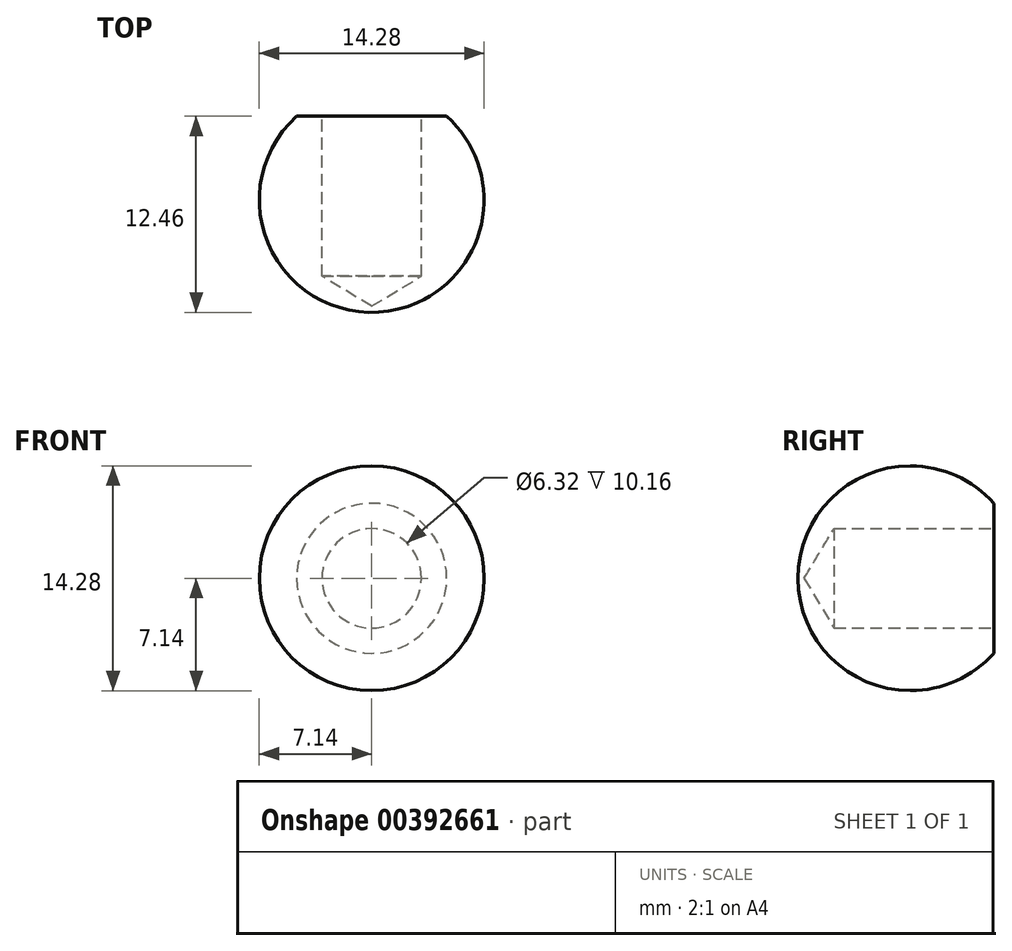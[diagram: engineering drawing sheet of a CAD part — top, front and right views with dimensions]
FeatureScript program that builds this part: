
annotation { "Feature Type Name" : "Feature", "Feature Type Description" : "" }
export const myFeature = defineFeature(function(context is Context, id is Id, definition is map)
    precondition{}
    {
        {
            var Q0;
            Q0=qCreatedBy(makeId("Front.planeOp"),FACE);
            var sketch = newSketch(context, id + "F0", { "sketchPlane" : qUnion([Q0])});
            skArc(sketch, "E0", {"start": v(0, -7.14) * mm, "mid": v(7.14, 0) * mm, "end": v(0, 7.14) * mm});
            skLineSegment(sketch, "E1", {"start": v(0, 7.14) * mm, "end": v(0, -7.14) * mm});
            skSolve(sketch);
        }
        {
            var Q0;
            Q0=makeQuery(id+"F0.imprint","IMPRINT",FACE,{"disambiguationData":[TD([[makeQuery(id+"F0.imprint","IMPRINT",EDGE,{"derivedFrom":sQuery(id+"F0.wireOp",EDGE,"E0")}),1.0]])]});
            var Q1;
            Q1=sQuery(id+"F0.wireOp",EDGE,"E1");
            revolve(context, id + "F1", {"entities" : qUnion([Q0]), "axis" : qUnion([Q1]), "revolveType" : RevolveType.FULL});
        }
        {
            var Q0;
            Q0=qCreatedBy(makeId("Top.planeOp"),FACE);
            var sketch = newSketch(context, id + "F2", { "sketchPlane" : qUnion([Q0])});
            skLineSegment(sketch, "E2", {"start": v(-4.76, 5.32) * mm, "end": v(4.76, 5.32) * mm});
            skArc(sketch, "E3", {"start": v(4.76, 5.32) * mm, "mid": v(0, 7.14) * mm, "end": v(-4.76, 5.32) * mm});
            skSolve(sketch);
        }
        {
            var Q0;
            Q0 = qSketchRegion(id + "F2", true);
            extrude(context, id + "F3", {"entities" : qUnion([Q0]), "operationType" : NewBodyOperationType.REMOVE, "endBound" : BoundingType.SYMMETRIC, "depth" : 25.4 * mm});
        }
        {
            var Q0;
            Q0=makeQuery(id+"F3.boolean.opBoolean","COPY",FACE,{"derivedFrom":makeQuery(id+"F3.opExtrude","SWEPT_FACE",FACE,{"disambiguationData":[OSD([sQuery(id+"F2.wireOp",EDGE,"E2")])]})});
            var sketch = newSketch(context, id + "F4", { "sketchPlane" : qUnion([Q0])});
            skPoint(sketch, "E4", {"position": v(0, 0) * mm});
            skSolve(sketch);
        }
        {
            var Q0;
            Q0=sQuery(id+"F4.wireOp",VERTEX,"E4");
            var Q1;
            Q1=makeQuery(id+"F1.opRevolve","SWEPT_BODY",BODY,{"disambiguationData":[OSD([sQuery(id+"F0.wireOp",EDGE,"E0"),sQuery(id+"F0.wireOp",EDGE,"E1")])]});
            hole(context, id + "F5", {"style" : HoleStyle.SIMPLE, "endStyle" : HoleEndStyle.BLIND, "holeDiameter" : 6.32 * mm, "holeDepth" : 10.16 * mm, "isTappedThrough" : true, "tappedDepth" : 12.7 * mm, "tapClearance" : 3, "locations" : qUnion([Q0]), "scope" : qUnion([Q1])});
        }
    });
